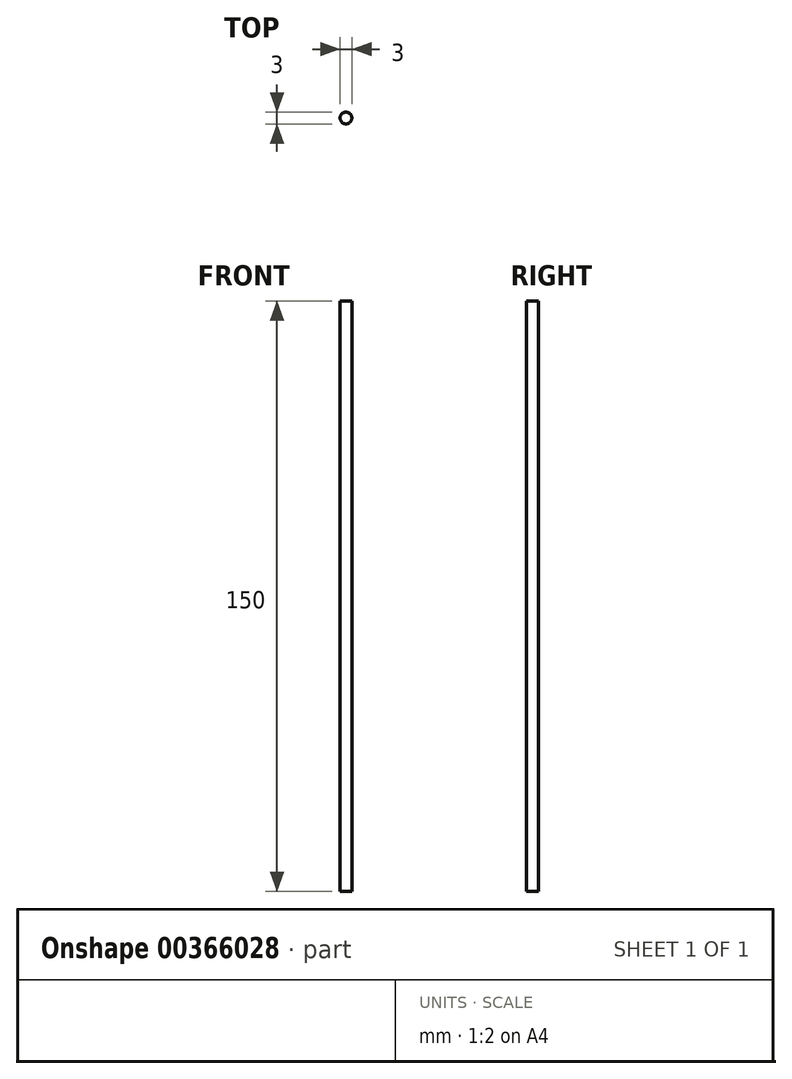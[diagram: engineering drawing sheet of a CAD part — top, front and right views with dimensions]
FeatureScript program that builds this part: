
annotation { "Feature Type Name" : "Feature", "Feature Type Description" : "" }
export const myFeature = defineFeature(function(context is Context, id is Id, definition is map)
    precondition{}
    {
        {
            var Q0;
            Q0=qCreatedBy(makeId("Top.planeOp"),FACE);
            var sketch = newSketch(context, id + "F0", { "sketchPlane" : qUnion([Q0])});
            skCircle(sketch, "E0", {"center": v(0, 0) * mm, "radius": 1.5 * mm});
            skSolve(sketch);
        }
        {
            var Q0;
            Q0=makeQuery(id+"F0.imprint","IMPRINT",FACE,{"disambiguationData":[TD([[makeQuery(id+"F0.imprint","IMPRINT",EDGE,{"derivedFrom":sQuery(id+"F0.wireOp",EDGE,"E0")}),1.0]])]});
            extrude(context, id + "F1", {"entities" : qUnion([Q0]), "depth" : 150 * mm});
        }
    });
